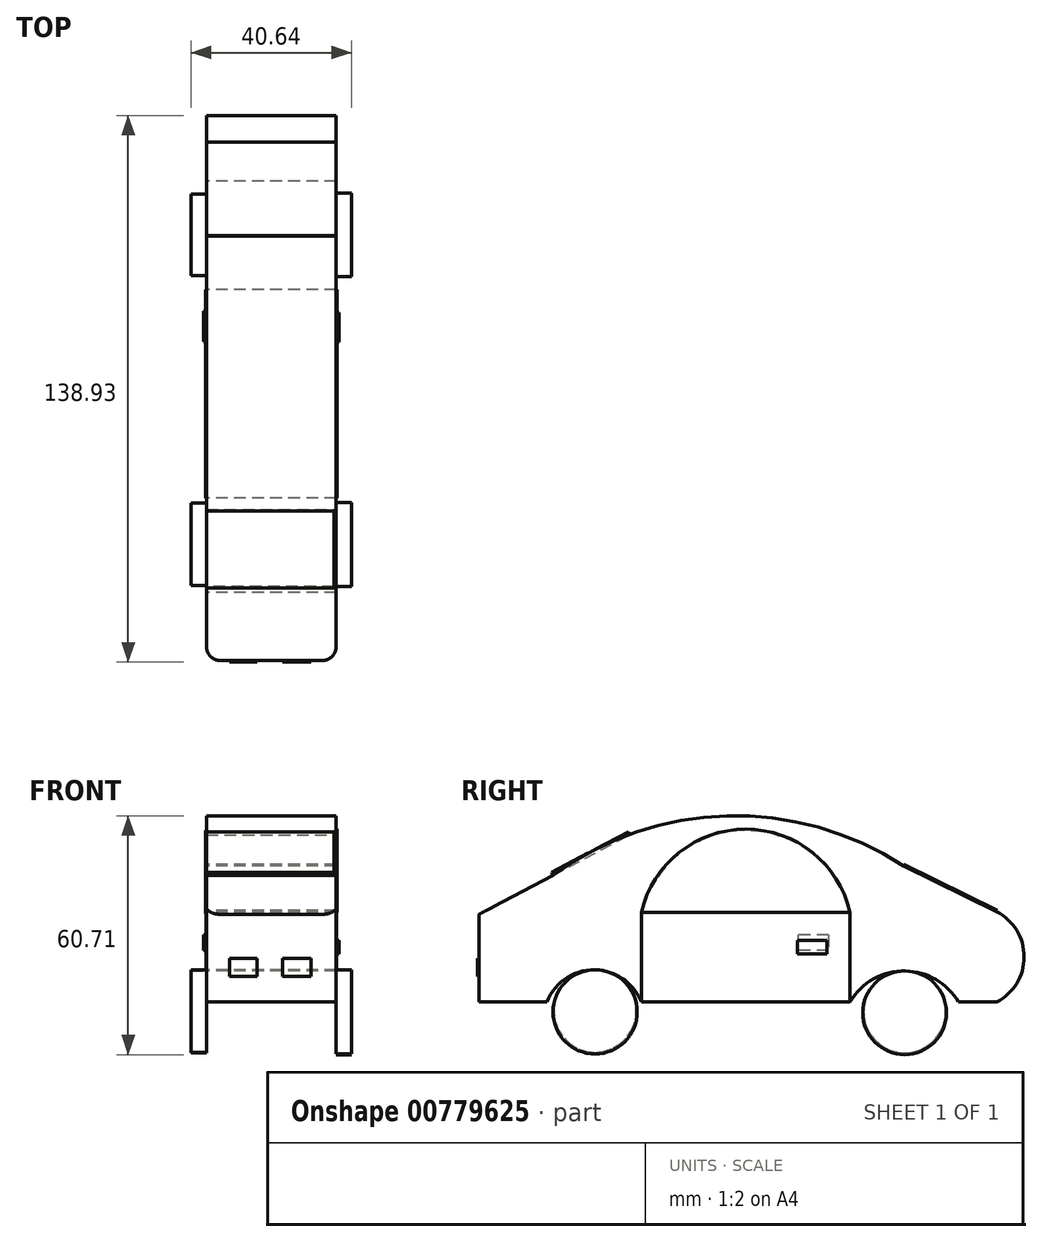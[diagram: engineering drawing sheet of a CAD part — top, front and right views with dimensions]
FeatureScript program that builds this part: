
annotation { "Feature Type Name" : "Feature", "Feature Type Description" : "" }
export const myFeature = defineFeature(function(context is Context, id is Id, definition is map)
    precondition{}
    {
        {
            var Q0;
            Q0=qCreatedBy(makeId("Right.planeOp"),FACE);
            var sketch = newSketch(context, id + "F0", { "sketchPlane" : qUnion([Q0])});
            skLineSegment(sketch, "E0", {"start": v(-72.05, -6.48) * mm, "end": v(-54.78, -6.48) * mm});
            skArc(sketch, "E1", {"start": v(-30.69, -6.48) * mm, "mid": v(-42.73, 1.72) * mm, "end": v(-54.78, -6.48) * mm});
            skLineSegment(sketch, "E2", {"start": v(-30.69, -6.48) * mm, "end": v(22.28, -6.48) * mm});
            skArc(sketch, "E3", {"start": v(49.78, -6.48) * mm, "mid": v(36.03, 1.43) * mm, "end": v(22.28, -6.48) * mm});
            skLineSegment(sketch, "E4", {"start": v(49.78, -6.48) * mm, "end": v(59.55, -6.48) * mm});
            skArc(sketch, "E5", {"start": v(59.55, -6.48) * mm, "mid": v(66.5, 5) * mm, "end": v(59.55, 16.48) * mm});
            skLineSegment(sketch, "E6", {"start": v(-72.05, -6.48) * mm, "end": v(-72.05, 15.8) * mm});
            skLineSegment(sketch, "E7", {"start": v(-72.05, 15.8) * mm, "end": v(-53.18, 25.75) * mm});
            skLineSegment(sketch, "E8", {"start": v(59.55, 16.48) * mm, "end": v(35.8, 28.12) * mm});
            skArc(sketch, "E9", {"start": v(35.8, 28.12) * mm, "mid": v(-9.06, 40.84) * mm, "end": v(-53.18, 25.75) * mm});
            skSolve(sketch);
        }
        {
            var Q0;
            Q0=makeQuery(id+"F0.imprint","IMPRINT",FACE,{"disambiguationData":[TD([[makeQuery(id+"F0.imprint","IMPRINT",EDGE,{"derivedFrom":sQuery(id+"F0.wireOp",EDGE,"E0")}),1.0]])]});
            extrude(context, id + "F1", {"entities" : qUnion([Q0]), "depth" : 33.02 * mm, "offsetDistance" : 25.4 * mm});
        }
        {
            var Q0;
            Q0=makeQuery(id+"F1.opExtrude","CAP_FACE",FACE,{"disambiguationData":[OSD([sQuery(id+"F0.wireOp",EDGE,"E0"),sQuery(id+"F0.wireOp",EDGE,"E1"),sQuery(id+"F0.wireOp",EDGE,"E2"),sQuery(id+"F0.wireOp",EDGE,"E3"),sQuery(id+"F0.wireOp",EDGE,"E4"),sQuery(id+"F0.wireOp",EDGE,"E5"),sQuery(id+"F0.wireOp",EDGE,"E6"),sQuery(id+"F0.wireOp",EDGE,"E7"),sQuery(id+"F0.wireOp",EDGE,"E8"),sQuery(id+"F0.wireOp",EDGE,"E9")])],"isStart":false});
            var sketch = newSketch(context, id + "F2", { "sketchPlane" : qUnion([Q0])});
            skCircle(sketch, "E10", {"center": v(-42.5, -8.98) * mm, "radius": 10.69 * mm});
            skCircle(sketch, "E11", {"center": v(36.14, -9.2) * mm, "radius": 10.63 * mm});
            skSolve(sketch);
        }
        {
            var Q0;
            Q0=makeQuery(id+"F1.opExtrude","CAP_FACE",FACE,{"disambiguationData":[OSD([sQuery(id+"F0.wireOp",EDGE,"E0"),sQuery(id+"F0.wireOp",EDGE,"E1"),sQuery(id+"F0.wireOp",EDGE,"E2"),sQuery(id+"F0.wireOp",EDGE,"E3"),sQuery(id+"F0.wireOp",EDGE,"E4"),sQuery(id+"F0.wireOp",EDGE,"E5"),sQuery(id+"F0.wireOp",EDGE,"E6"),sQuery(id+"F0.wireOp",EDGE,"E7"),sQuery(id+"F0.wireOp",EDGE,"E8"),sQuery(id+"F0.wireOp",EDGE,"E9")])],"isStart":true});
            var sketch = newSketch(context, id + "F3", { "sketchPlane" : qUnion([Q0])});
            skCircle(sketch, "E12", {"center": v(-36.03, -9.2) * mm, "radius": 10.63 * mm});
            skPoint(sketch, "E12.centerSnap0", {"position": v(-36.03, 1.43) * mm});
            skCircle(sketch, "E13", {"center": v(42.5, -8.75) * mm, "radius": 10.46 * mm});
            skSolve(sketch);
        }
        {
            var Q0;
            Q0=makeQuery(id+"F3.imprint","IMPRINT",FACE,{"disambiguationData":[TD([[makeQuery(id+"F3.imprint","IMPRINT",EDGE,{"derivedFrom":sQuery(id+"F3.wireOp",EDGE,"E13")}),1.0]])]});
            extrude(context, id + "F4", {"entities" : qUnion([Q0]), "depth" : 3.8 * mm, "offsetDistance" : 25.4 * mm});
        }
        {
            var Q0;
            Q0=makeQuery(id+"F1.opExtrude","CAP_FACE",FACE,{"disambiguationData":[OSD([sQuery(id+"F0.wireOp",EDGE,"E0"),sQuery(id+"F0.wireOp",EDGE,"E1"),sQuery(id+"F0.wireOp",EDGE,"E2"),sQuery(id+"F0.wireOp",EDGE,"E3"),sQuery(id+"F0.wireOp",EDGE,"E4"),sQuery(id+"F0.wireOp",EDGE,"E5"),sQuery(id+"F0.wireOp",EDGE,"E6"),sQuery(id+"F0.wireOp",EDGE,"E7"),sQuery(id+"F0.wireOp",EDGE,"E8"),sQuery(id+"F0.wireOp",EDGE,"E9")])],"isStart":true});
            var sketch = newSketch(context, id + "F5", { "sketchPlane" : qUnion([Q0])});
            skCircle(sketch, "E14", {"center": v(-36.14, -8.98) * mm, "radius": 10.4 * mm});
            skSolve(sketch);
        }
        {
            var Q0;
            Q0=makeQuery(id+"F5.imprint","IMPRINT",FACE,{"disambiguationData":[TD([[makeQuery(id+"F5.imprint","IMPRINT",EDGE,{"derivedFrom":sQuery(id+"F5.wireOp",EDGE,"E14")}),1.0]])]});
            extrude(context, id + "F6", {"entities" : qUnion([Q0]), "depth" : 3.8 * mm, "offsetDistance" : 25.4 * mm});
        }
        {
            var Q0;
            Q0=makeQuery(id+"F2.imprint","IMPRINT",FACE,{"disambiguationData":[TD([[makeQuery(id+"F2.imprint","IMPRINT",EDGE,{"derivedFrom":sQuery(id+"F2.wireOp",EDGE,"E11")}),1.0]])]});
            extrude(context, id + "F7", {"entities" : qUnion([Q0]), "depth" : 3.8 * mm, "offsetDistance" : 25.4 * mm});
        }
        {
            var Q0;
            Q0=makeQuery(id+"F2.imprint","IMPRINT",FACE,{"disambiguationData":[TD([[makeQuery(id+"F2.imprint","IMPRINT",EDGE,{"derivedFrom":sQuery(id+"F2.wireOp",EDGE,"E10")}),1.0]])]});
            extrude(context, id + "F8", {"entities" : qUnion([Q0]), "depth" : 3.8 * mm, "offsetDistance" : 25.4 * mm});
        }
        {
            var Q0;
            Q0=makeQuery(id+"F1.opExtrude","CAP_FACE",FACE,{"disambiguationData":[OSD([sQuery(id+"F0.wireOp",EDGE,"E0"),sQuery(id+"F0.wireOp",EDGE,"E1"),sQuery(id+"F0.wireOp",EDGE,"E2"),sQuery(id+"F0.wireOp",EDGE,"E3"),sQuery(id+"F0.wireOp",EDGE,"E4"),sQuery(id+"F0.wireOp",EDGE,"E5"),sQuery(id+"F0.wireOp",EDGE,"E6"),sQuery(id+"F0.wireOp",EDGE,"E7"),sQuery(id+"F0.wireOp",EDGE,"E8"),sQuery(id+"F0.wireOp",EDGE,"E9")])],"isStart":true});
            var sketch = newSketch(context, id + "F9", { "sketchPlane" : qUnion([Q0])});
            skLineSegment(sketch, "E15.bottom", {"start": v(-22.28, -6.48) * mm, "end": v(3.36, -6.48) * mm});
            skLineSegment(sketch, "E15.top", {"start": v(-22.28, 16.09) * mm, "end": v(3.36, 16.09) * mm});
            skLineSegment(sketch, "E15.left", {"start": v(-22.28, -6.48) * mm, "end": v(-22.28, 16.09) * mm});
            skLineSegment(sketch, "E15.right", {"start": v(3.36, -6.48) * mm, "end": v(3.36, 16.09) * mm});
            skLineSegment(sketch, "E16.bottom", {"start": v(3.36, 16.09) * mm, "end": v(30.69, 16.09) * mm});
            skLineSegment(sketch, "E16.top", {"start": v(3.36, -6.48) * mm, "end": v(30.69, -6.48) * mm});
            skLineSegment(sketch, "E16.left", {"start": v(3.36, 16.09) * mm, "end": v(3.36, -6.48) * mm});
            skLineSegment(sketch, "E16.right", {"start": v(30.69, 16.09) * mm, "end": v(30.69, -6.48) * mm});
            skSolve(sketch);
        }
        {
            var Q0;
            Q0=makeQuery(id+"F9.imprint","IMPRINT",FACE,{"disambiguationData":[TD([[makeQuery(id+"F9.imprint","IMPRINT",EDGE,{"derivedFrom":sQuery(id+"F9.wireOp",EDGE,"E16.bottom")}),-1.0]])]});
            var Q1;
            Q1=makeQuery(id+"F9.imprint","IMPRINT",FACE,{"disambiguationData":[TD([[makeQuery(id+"F9.imprint","IMPRINT",EDGE,{"derivedFrom":sQuery(id+"F9.wireOp",EDGE,"E15.bottom")}),-1.0]])]});
            extrude(context, id + "F10", {"entities" : qUnion([Q0, Q1]), "operationType" : NewBodyOperationType.ADD, "depth" : 0.13 * mm, "offsetDistance" : 25.4 * mm});
        }
        {
            var Q0;
            Q0=makeQuery(id+"F10.opExtrude","CAP_FACE",FACE,{"disambiguationData":[OSD([sQuery(id+"F9.wireOp",EDGE,"E15.bottom"),sQuery(id+"F9.wireOp",EDGE,"E15.top"),sQuery(id+"F9.wireOp",EDGE,"E15.left"),sQuery(id+"F9.wireOp",EDGE,"E16.bottom"),sQuery(id+"F9.wireOp",EDGE,"E16.top"),sQuery(id+"F9.wireOp",EDGE,"E16.right")])],"isStart":false});
            var sketch = newSketch(context, id + "F11", { "sketchPlane" : qUnion([Q0])});
            skArc(sketch, "E17", {"start": v(30.69, 16.09) * mm, "mid": v(4.2, 37.12) * mm, "end": v(-22.28, 16.09) * mm});
            skSolve(sketch);
        }
        {
            var Q0;
            Q0=makeQuery(id+"F11.imprint","IMPRINT",FACE,{"disambiguationData":[TD([[makeQuery(id+"F11.imprint","IMPRINT",EDGE,{"derivedFrom":sQuery(id+"F11.wireOp",EDGE,"E17")}),1.0]])]});
            extrude(context, id + "F12", {"entities" : qUnion([Q0]), "depth" : 0.13 * mm, "offsetDistance" : 25.4 * mm});
        }
        {
            var Q0;
            Q0=makeQuery(id+"F1.opExtrude","CAP_FACE",FACE,{"disambiguationData":[OSD([sQuery(id+"F0.wireOp",EDGE,"E0"),sQuery(id+"F0.wireOp",EDGE,"E1"),sQuery(id+"F0.wireOp",EDGE,"E2"),sQuery(id+"F0.wireOp",EDGE,"E3"),sQuery(id+"F0.wireOp",EDGE,"E4"),sQuery(id+"F0.wireOp",EDGE,"E5"),sQuery(id+"F0.wireOp",EDGE,"E6"),sQuery(id+"F0.wireOp",EDGE,"E7"),sQuery(id+"F0.wireOp",EDGE,"E8"),sQuery(id+"F0.wireOp",EDGE,"E9")])],"isStart":false});
            var sketch = newSketch(context, id + "F13", { "sketchPlane" : qUnion([Q0])});
            skLineSegment(sketch, "E18.bottom", {"start": v(22.28, -6.48) * mm, "end": v(-5.04, -6.48) * mm});
            skLineSegment(sketch, "E18.top", {"start": v(22.28, 16.37) * mm, "end": v(-5.04, 16.37) * mm});
            skLineSegment(sketch, "E18.left", {"start": v(22.28, -6.48) * mm, "end": v(22.28, 16.37) * mm});
            skLineSegment(sketch, "E18.right", {"start": v(-5.04, -6.48) * mm, "end": v(-5.04, 16.37) * mm});
            skLineSegment(sketch, "E19.bottom", {"start": v(-30.69, -6.48) * mm, "end": v(-5.04, -6.48) * mm});
            skLineSegment(sketch, "E19.top", {"start": v(-30.69, 16.37) * mm, "end": v(-5.04, 16.37) * mm});
            skLineSegment(sketch, "E19.left", {"start": v(-30.69, -6.48) * mm, "end": v(-30.69, 16.37) * mm});
            skSolve(sketch);
        }
        {
            var Q0;
            Q0=makeQuery(id+"F13.imprint","IMPRINT",FACE,{"disambiguationData":[TD([[makeQuery(id+"F13.imprint","IMPRINT",EDGE,{"derivedFrom":sQuery(id+"F13.wireOp",EDGE,"E19.bottom")}),1.0]])]});
            var Q1;
            Q1=makeQuery(id+"F13.imprint","IMPRINT",FACE,{"disambiguationData":[TD([[makeQuery(id+"F13.imprint","IMPRINT",EDGE,{"derivedFrom":sQuery(id+"F13.wireOp",EDGE,"E18.bottom")}),1.0]])]});
            extrude(context, id + "F14", {"entities" : qUnion([Q0, Q1]), "operationType" : NewBodyOperationType.ADD, "depth" : 0.13 * mm, "offsetDistance" : 25.4 * mm});
        }
        {
            var Q0;
            Q0=makeQuery(id+"F14.opExtrude","CAP_FACE",FACE,{"disambiguationData":[OSD([sQuery(id+"F13.wireOp",EDGE,"E18.bottom"),sQuery(id+"F13.wireOp",EDGE,"E18.top"),sQuery(id+"F13.wireOp",EDGE,"E18.left"),sQuery(id+"F13.wireOp",EDGE,"E19.bottom"),sQuery(id+"F13.wireOp",EDGE,"E19.top"),sQuery(id+"F13.wireOp",EDGE,"E19.left")])],"isStart":false});
            var sketch = newSketch(context, id + "F15", { "sketchPlane" : qUnion([Q0])});
            skArc(sketch, "E20", {"start": v(22.28, 16.37) * mm, "mid": v(-4.2, 37.47) * mm, "end": v(-30.69, 16.37) * mm});
            skSolve(sketch);
        }
        {
            var Q0;
            Q0=makeQuery(id+"F15.imprint","IMPRINT",FACE,{"disambiguationData":[TD([[makeQuery(id+"F15.imprint","IMPRINT",EDGE,{"derivedFrom":sQuery(id+"F15.wireOp",EDGE,"E20")}),1.0]])]});
            extrude(context, id + "F16", {"entities" : qUnion([Q0]), "depth" : 0.13 * mm, "offsetDistance" : 25.4 * mm});
        }
        {
            var Q0;
            Q0=makeQuery(id+"F1.opExtrude","CAP_EDGE",EDGE,{"disambiguationData":[OSD([sQuery(id+"F0.wireOp",EDGE,"E6")])],"isStart":false});
            var Q1;
            Q1=makeQuery(id+"F1.opExtrude","CAP_EDGE",EDGE,{"disambiguationData":[OSD([sQuery(id+"F0.wireOp",EDGE,"E6")])],"isStart":true});
            fillet(context, id + "F17", {"entities" : qUnion([Q0, Q1]), "radius" : 3.68 * mm, "tangentPropagation" : true, "allowEdgeOverflow" : false});
        }
        {
            var Q0;
            Q0=makeQuery(id+"F10.opExtrude","CAP_FACE",FACE,{"disambiguationData":[OSD([sQuery(id+"F9.wireOp",EDGE,"E15.bottom"),sQuery(id+"F9.wireOp",EDGE,"E15.top"),sQuery(id+"F9.wireOp",EDGE,"E15.left"),sQuery(id+"F9.wireOp",EDGE,"E16.bottom"),sQuery(id+"F9.wireOp",EDGE,"E16.top"),sQuery(id+"F9.wireOp",EDGE,"E16.right")])],"isStart":false});
            var sketch = newSketch(context, id + "F18", { "sketchPlane" : qUnion([Q0])});
            skLineSegment(sketch, "E21.bottom", {"start": v(-16.82, 10.57) * mm, "end": v(-9.1, 10.57) * mm});
            skLineSegment(sketch, "E21.top", {"start": v(-16.82, 6.7) * mm, "end": v(-9.1, 6.7) * mm});
            skLineSegment(sketch, "E21.left", {"start": v(-16.82, 10.57) * mm, "end": v(-16.82, 6.7) * mm});
            skLineSegment(sketch, "E21.right", {"start": v(-9.1, 10.57) * mm, "end": v(-9.1, 6.7) * mm});
            skSolve(sketch);
        }
        {
            var Q0;
            Q0=makeQuery(id+"F18.imprint","IMPRINT",FACE,{"disambiguationData":[TD([[makeQuery(id+"F18.imprint","IMPRINT",EDGE,{"derivedFrom":sQuery(id+"F18.wireOp",EDGE,"E21.bottom")}),-1.0]])]});
            extrude(context, id + "F19", {"entities" : qUnion([Q0]), "operationType" : NewBodyOperationType.ADD, "depth" : 0.5 * mm, "offsetDistance" : 25.4 * mm});
        }
        {
            var Q0;
            Q0=makeQuery(id+"F14.opExtrude","CAP_FACE",FACE,{"disambiguationData":[OSD([sQuery(id+"F13.wireOp",EDGE,"E18.bottom"),sQuery(id+"F13.wireOp",EDGE,"E18.top"),sQuery(id+"F13.wireOp",EDGE,"E18.left"),sQuery(id+"F13.wireOp",EDGE,"E19.bottom"),sQuery(id+"F13.wireOp",EDGE,"E19.top"),sQuery(id+"F13.wireOp",EDGE,"E19.left")])],"isStart":false});
            var sketch = newSketch(context, id + "F20", { "sketchPlane" : qUnion([Q0])});
            skLineSegment(sketch, "E22.bottom", {"start": v(8.86, 9.2) * mm, "end": v(16.37, 9.2) * mm});
            skLineSegment(sketch, "E22.top", {"start": v(8.86, 5.8) * mm, "end": v(16.37, 5.8) * mm});
            skLineSegment(sketch, "E22.left", {"start": v(8.86, 9.2) * mm, "end": v(8.86, 5.8) * mm});
            skLineSegment(sketch, "E22.right", {"start": v(16.37, 9.2) * mm, "end": v(16.37, 5.8) * mm});
            skSolve(sketch);
        }
        {
            var Q0;
            Q0=makeQuery(id+"F20.imprint","IMPRINT",FACE,{"disambiguationData":[TD([[makeQuery(id+"F20.imprint","IMPRINT",EDGE,{"derivedFrom":sQuery(id+"F20.wireOp",EDGE,"E22.bottom")}),-1.0]])]});
            extrude(context, id + "F21", {"entities" : qUnion([Q0]), "operationType" : NewBodyOperationType.ADD, "depth" : 0.5 * mm, "offsetDistance" : 25.4 * mm});
        }
        {
            var Q0;
            Q0=makeQuery(id+"F1.opExtrude","SWEPT_FACE",FACE,{"disambiguationData":[OSD([sQuery(id+"F0.wireOp",EDGE,"E8")])]});
            var sketch = newSketch(context, id + "F22", { "sketchPlane" : qUnion([Q0])});
            skLineSegment(sketch, "E23.bottom", {"start": v(0, 19.78) * mm, "end": v(33.02, 19.78) * mm});
            skLineSegment(sketch, "E23.top", {"start": v(0, 46.22) * mm, "end": v(33.02, 46.22) * mm});
            skLineSegment(sketch, "E23.left", {"start": v(0, 19.78) * mm, "end": v(0, 46.22) * mm});
            skLineSegment(sketch, "E23.right", {"start": v(33.02, 19.78) * mm, "end": v(33.02, 46.22) * mm});
            skSolve(sketch);
        }
        {
            var Q0;
            Q0 = qSketchRegion(id + "F22", true);
            extrude(context, id + "F23", {"entities" : qUnion([Q0]), "depth" : 0.38 * mm, "offsetDistance" : 25.4 * mm});
        }
        {
            var Q0;
            Q0=makeQuery(id+"F1.opExtrude","SWEPT_FACE",FACE,{"disambiguationData":[OSD([sQuery(id+"F0.wireOp",EDGE,"E6")])]});
            var sketch = newSketch(context, id + "F24", { "sketchPlane" : qUnion([Q0])});
            skPoint(sketch, "E24.firstSnap0", {"position": v(29.34, 4.66) * mm});
            skLineSegment(sketch, "E24.bottom", {"start": v(5.9, 4.66) * mm, "end": v(12.96, 4.66) * mm});
            skLineSegment(sketch, "E24.top", {"start": v(5.9, 0) * mm, "end": v(12.96, 0) * mm});
            skLineSegment(sketch, "E24.left", {"start": v(5.9, 4.66) * mm, "end": v(5.9, 0) * mm});
            skLineSegment(sketch, "E24.right", {"start": v(12.96, 4.66) * mm, "end": v(12.96, 0) * mm});
            skLineSegment(sketch, "E25.bottom", {"start": v(19.32, 4.66) * mm, "end": v(26.6, 4.66) * mm});
            skLineSegment(sketch, "E25.top", {"start": v(19.32, 0) * mm, "end": v(26.6, 0) * mm});
            skLineSegment(sketch, "E25.left", {"start": v(19.32, 4.66) * mm, "end": v(19.32, 0) * mm});
            skLineSegment(sketch, "E25.right", {"start": v(26.6, 4.66) * mm, "end": v(26.6, 0) * mm});
            skSolve(sketch);
        }
        {
            var Q0;
            Q0=makeQuery(id+"F24.imprint","IMPRINT",FACE,{"disambiguationData":[TD([[makeQuery(id+"F24.imprint","IMPRINT",EDGE,{"derivedFrom":sQuery(id+"F24.wireOp",EDGE,"E24.bottom")}),-1.0]])]});
            var Q1;
            Q1=makeQuery(id+"F24.imprint","IMPRINT",FACE,{"disambiguationData":[TD([[makeQuery(id+"F24.imprint","IMPRINT",EDGE,{"derivedFrom":sQuery(id+"F24.wireOp",EDGE,"E25.bottom")}),-1.0]])]});
            extrude(context, id + "F25", {"entities" : qUnion([Q0, Q1]), "depth" : 0.38 * mm, "offsetDistance" : 25.4 * mm});
        }
        {
            var Q0;
            Q0=makeQuery(id+"F1.opExtrude","SWEPT_FACE",FACE,{"disambiguationData":[OSD([sQuery(id+"F0.wireOp",EDGE,"E7")])]});
            var sketch = newSketch(context, id + "F26", { "sketchPlane" : qUnion([Q0])});
            skLineSegment(sketch, "E26.bottom", {"start": v(0, -35.03) * mm, "end": v(32.42, -35.03) * mm});
            skLineSegment(sketch, "E26.top", {"start": v(0, -12.96) * mm, "end": v(32.42, -12.96) * mm});
            skLineSegment(sketch, "E26.left", {"start": v(0, -35.03) * mm, "end": v(0, -12.96) * mm});
            skLineSegment(sketch, "E26.right", {"start": v(32.42, -35.03) * mm, "end": v(32.42, -12.96) * mm});
            skSolve(sketch);
        }
        {
            var Q0;
            Q0 = qSketchRegion(id + "F26", true);
            extrude(context, id + "F27", {"entities" : qUnion([Q0]), "depth" : 0.84 * mm, "offsetDistance" : 25.4 * mm});
        }
    });
